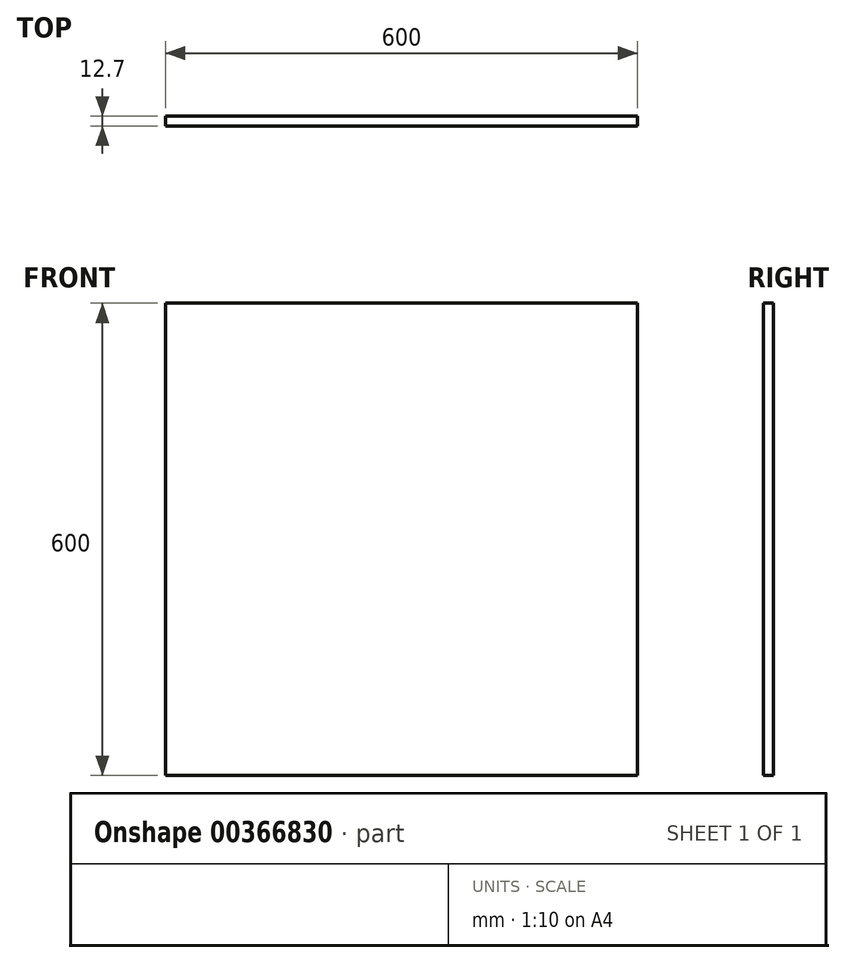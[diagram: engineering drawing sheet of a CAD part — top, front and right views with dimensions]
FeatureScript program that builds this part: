
annotation { "Feature Type Name" : "Feature", "Feature Type Description" : "" }
export const myFeature = defineFeature(function(context is Context, id is Id, definition is map)
    precondition{}
    {
        {
            var Q0;
            Q0=qCreatedBy(makeId("Front.planeOp"),FACE);
            var sketch = newSketch(context, id + "F0", { "sketchPlane" : qUnion([Q0])});
            skLineSegment(sketch, "E0.bottom", {"start": v(-665.94, 566.97) * mm, "end": v(-65.94, 566.97) * mm});
            skLineSegment(sketch, "E0.top", {"start": v(-665.94, -33.03) * mm, "end": v(-65.94, -33.03) * mm});
            skLineSegment(sketch, "E0.left", {"start": v(-665.94, 566.97) * mm, "end": v(-665.94, -33.03) * mm});
            skLineSegment(sketch, "E0.right", {"start": v(-65.94, 566.97) * mm, "end": v(-65.94, -33.03) * mm});
            skSolve(sketch);
        }
        {
            var Q0;
            Q0=makeQuery(id+"F0.imprint","IMPRINT",FACE,{"disambiguationData":[TD([[makeQuery(id+"F0.imprint","IMPRINT",EDGE,{"derivedFrom":sQuery(id+"F0.wireOp",EDGE,"E0.bottom")}),-1.0]])]});
            extrude(context, id + "F1", {"entities" : qUnion([Q0]), "depth" : 12.7 * mm});
        }
    });
